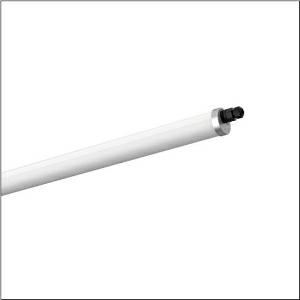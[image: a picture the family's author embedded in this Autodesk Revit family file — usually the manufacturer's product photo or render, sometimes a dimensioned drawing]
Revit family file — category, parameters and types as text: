
# Revit family: monsun_31_tube_51ft107n4a0a
name_source: partatom
category: Lighting Fixtures
units: mm (PartAtom-declared; Revit-internal decimal feet)

## family parameters
Cut with Voids When Loaded = No
Host = Face
Light Source = No
Part Type = Normal
Room Calculation Point = No
Round Connector Dimension = Use Diameter
Shared = No

## types (1)
- Monsun 31 Tube (1 x LED, 10000 lm, 58 W, 4000K)
    Apparent Load = 58 VA
    CIE Flux Codes = 42 71 90 91 100
    Color Rendering = 80
    Color Temperature = 4000K
    Default Elevation = 1800 mm
    Description = Monsun 31 Tube, tubular luminaire, primary optical cover: diffuser, of PMMA, light emission: direct distribution, primary light characteristic: symmetric, installation type: suspended mounting, surface-mounted, LED, rated luminous flux: 10.000lm, luminous efficacy: 160lm/W, light colour: 840, colour temperature: 4000K, control gear: ON/OFF, with with 1 terminal, 3-pole, max. 2.5mm², through-wiring: 3x 1.5mm², mains connection: 220..240V, AC, 50/60Hz, rated input power: 58W, housing, cylindrical, of PMMA, semi-transparent, matt white, with luminaire and ceiling fastening, V4A, mounting with brackets of stainless steel, length: 1.560mm, diameter: 75mm, end cap, of stainless steel (V4A), protection rating (complete): IP67/IP69K, insulation class (complete): insulation class I (protective earthing), certification: CE, UKCA, impact resistance: IK07, permissible operating ambient temperature: -20..+40°C, corresponds to IFS (International Featured Standards) requirements for safety and quality in the food industry, usage in unprotected outdoor areas possible with horizontal mounting, contact your sales advisor before using the luminaires in applications with unclear chemical exposure, large temperature fluctuations or condensation-forming humidity, packaging unit: 1 piece
    Height = 83 mm
    Lamp = 1 x LED
    Lamp Light Flux = 10000 lm
    Lamp Power = 58 W
    Lamp count = 1
    Length = 1560 mm
    Luminous efficacy = 172 lm/W
    Manufacturer = Siteco
    ModVariant = No
    Model = 51FT107N4A0A
    Mounting Place = Ceiling
    Mounting Type = Pendant
    Number of Poles = 1
    OnlyDefault = Yes
    Power Factor = 1
    Product Name = Monsun 31 Tube
    Product group = tubular luminaire
    ProductGroupID = 906
    Protection Class = Protection class I
    RLX_Detail_Level = 1
    RLX_Emergency_Light_Flux = 0 lm
    RLX_Emergency_Type = 0
    RLX_Emergency_Type_DB = No
    RlxData = <blob elided: 25385 chars, md5=5cde6897>
    Socket = socket
    Standby Power = 0 W
    System Light Flux = 10000 lm
    System Power = 58 W
    Type Comments = Product without accessories
    Type Image = l_1228461.jpg
    URL = http://relux.com
    VarID = ---
    Voltage = 0 V
    Weight = 0.00 kg
    Width = 75 mm

## geometry (parser evidence)
native form markers: Blend x4, Sweep x14
no freeform markers — native parametric forms only
